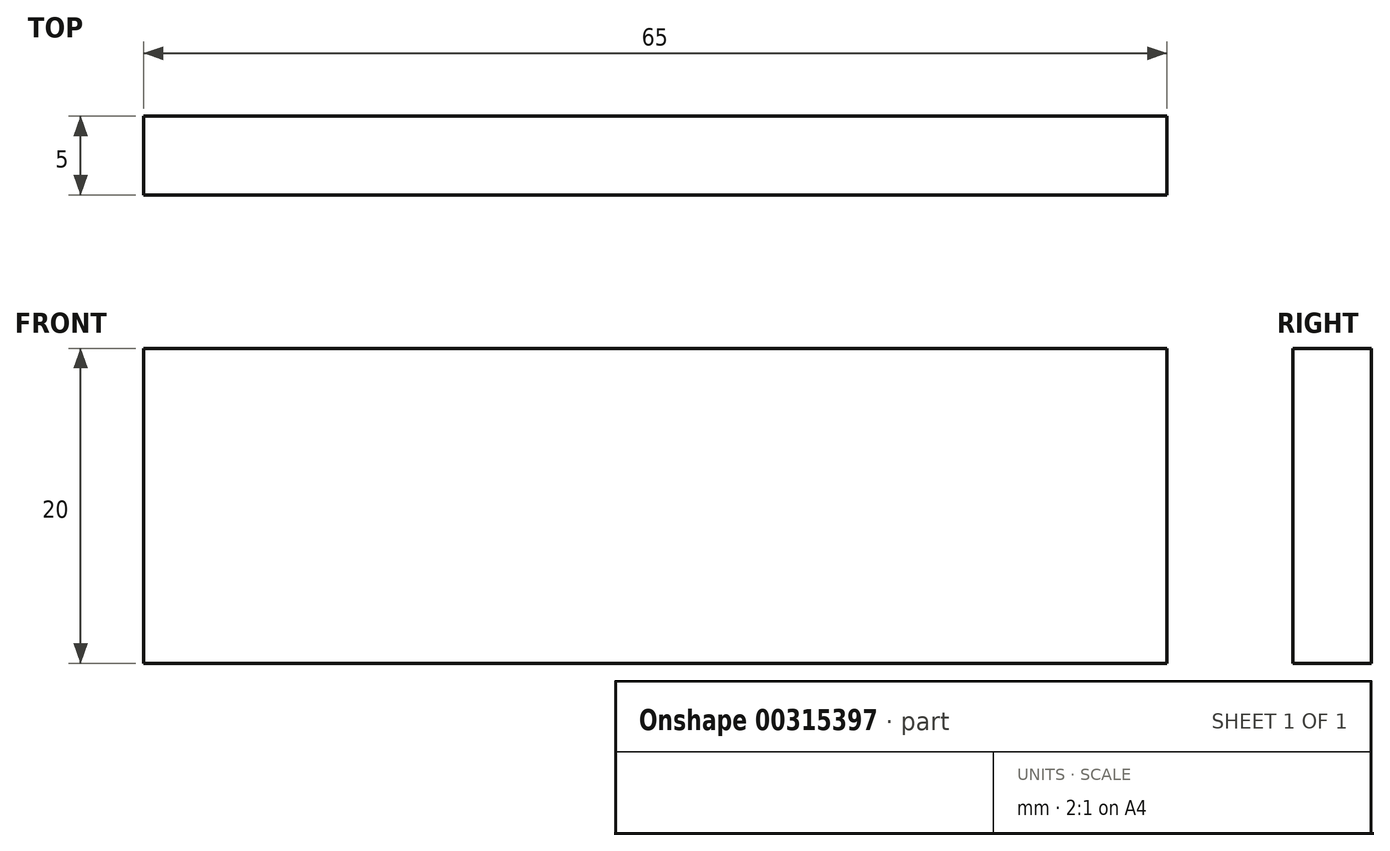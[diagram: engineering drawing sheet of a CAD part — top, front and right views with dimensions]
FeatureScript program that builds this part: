
annotation { "Feature Type Name" : "Feature", "Feature Type Description" : "" }
export const myFeature = defineFeature(function(context is Context, id is Id, definition is map)
    precondition{}
    {
        {
            var Q0;
            Q0=qCreatedBy(makeId("Front.planeOp"),FACE);
            var sketch = newSketch(context, id + "F0", { "sketchPlane" : qUnion([Q0])});
            skLineSegment(sketch, "E0.bottom", {"start": v(-31.04, 10) * mm, "end": v(33.96, 10) * mm});
            skLineSegment(sketch, "E0.top", {"start": v(-31.04, -10) * mm, "end": v(33.96, -10) * mm});
            skLineSegment(sketch, "E0.left", {"start": v(-31.04, 10) * mm, "end": v(-31.04, -10) * mm});
            skLineSegment(sketch, "E0.right", {"start": v(33.96, 10) * mm, "end": v(33.96, -10) * mm});
            skPoint(sketch, "E0.middle", {"position": v(1.46, 0) * mm});
            skSolve(sketch);
        }
        {
            var Q0;
            Q0=makeQuery(id+"F0.imprint","IMPRINT",FACE,{"disambiguationData":[TD([[makeQuery(id+"F0.imprint","IMPRINT",EDGE,{"derivedFrom":sQuery(id+"F0.wireOp",EDGE,"E0.bottom")}),-1.0]])]});
            extrude(context, id + "F1", {"entities" : qUnion([Q0]), "depth" : 5 * mm});
        }
    });
